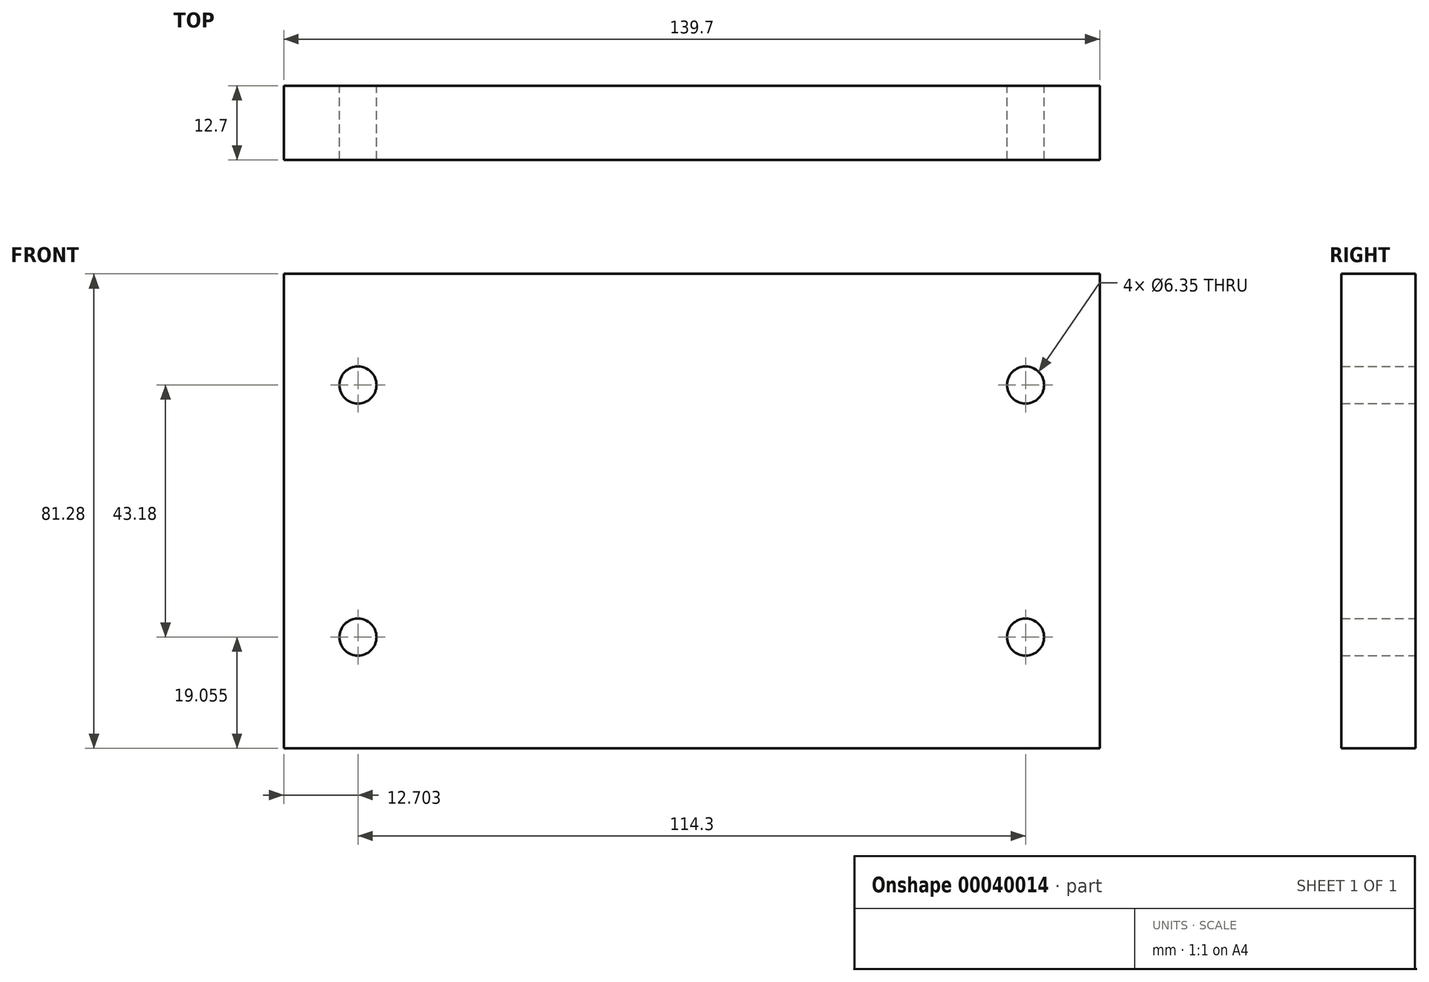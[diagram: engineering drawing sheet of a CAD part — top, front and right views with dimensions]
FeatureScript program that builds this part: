
annotation { "Feature Type Name" : "Feature", "Feature Type Description" : "" }
export const myFeature = defineFeature(function(context is Context, id is Id, definition is map)
    precondition{}
    {
        {
            var Q0;
            Q0=qCreatedBy(makeId("Front.planeOp"),FACE);
            var sketch = newSketch(context, id + "F0", { "sketchPlane" : qUnion([Q0])});
            skLineSegment(sketch, "E0.bottom", {"start": v(-68.76, 26.75) * mm, "end": v(70.94, 26.75) * mm});
            skLineSegment(sketch, "E0.top", {"start": v(-68.76, -54.53) * mm, "end": v(70.94, -54.53) * mm});
            skLineSegment(sketch, "E0.left", {"start": v(-68.76, 26.75) * mm, "end": v(-68.76, -54.53) * mm});
            skLineSegment(sketch, "E0.right", {"start": v(70.94, 26.75) * mm, "end": v(70.94, -54.53) * mm});
            skCircle(sketch, "E1", {"center": v(-56.06, 7.7) * mm, "radius": 3.18 * mm});
            skCircle(sketch, "E2", {"center": v(-56.06, -35.48) * mm, "radius": 3.18 * mm});
            skPoint(sketch, "E3.orphan", {"position": v(-56.06, 26.75) * mm});
            skPoint(sketch, "E4.orphan", {"position": v(-56.06, -54.53) * mm});
            skLineSegment(sketch, "E5", {"start": v(1.1, 26.75) * mm, "end": v(1.1, -54.53) * mm});
            skCircle(sketch, "E6.MirrorC", {"center": v(58.24, 7.7) * mm, "radius": 3.18 * mm});
            skCircle(sketch, "E7.MirrorC", {"center": v(58.24, -35.48) * mm, "radius": 3.18 * mm});
            skSolve(sketch);
        }
        {
            var Q0;
            Q0=makeQuery(id+"F0.imprint","IMPRINT",FACE,{"disambiguationData":[TD([[makeQuery(id+"F0.imprint","IMPRINT",EDGE,{"derivedFrom":sQuery(id+"F0.wireOp",EDGE,"E0.bottom")}),-1.0]])]});
            extrude(context, id + "F1", {"entities" : qUnion([Q0]), "depth" : 12.7 * mm});
        }
    });
